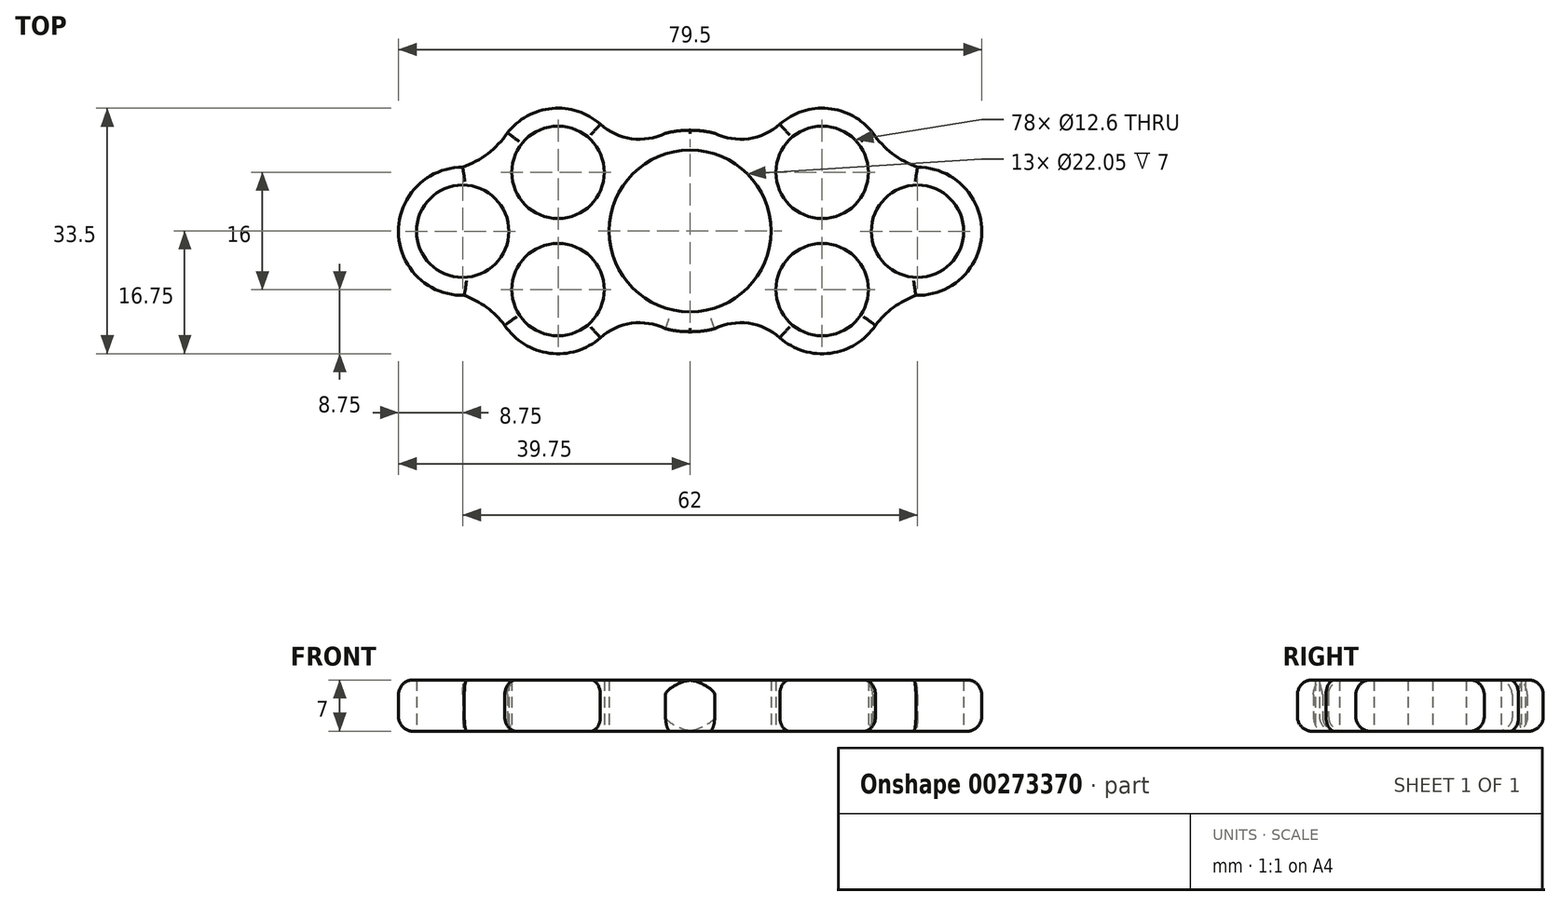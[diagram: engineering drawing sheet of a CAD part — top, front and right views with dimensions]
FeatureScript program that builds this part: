
annotation { "Feature Type Name" : "Feature", "Feature Type Description" : "" }
export const myFeature = defineFeature(function(context is Context, id is Id, definition is map)
    precondition{}
    {
        {
            var Q0;
            Q0=qCreatedBy(makeId("Top.planeOp"),FACE);
            var sketch = newSketch(context, id + "F0", { "sketchPlane" : qUnion([Q0])});
            skCircle(sketch, "E0", {"center": v(0, 0) * mm, "radius": 11.03 * mm});
            skCircle(sketch, "E1", {"center": v(18, 8) * mm, "radius": 6.3 * mm});
            skCircle(sketch, "E2.MirrorC", {"center": v(18, -8) * mm, "radius": 6.3 * mm});
            skLineSegment(sketch, "E3", {"start": v(18, -8) * mm, "end": v(18, 8) * mm, "construction": true});
            skCircle(sketch, "E4", {"center": v(31, -0.04) * mm, "radius": 6.3 * mm});
            skArc(sketch, "E5", {"start": v(3.35, 13.34) * mm, "mid": v(0, 13.75) * mm, "end": v(-3.35, 13.34) * mm});
            skArc(sketch, "E6", {"start": v(30.77, -8.79) * mm, "mid": v(39.75, -0.15) * mm, "end": v(31, 8.7) * mm});
            skArc(sketch, "E7", {"start": v(3.35, 13.34) * mm, "mid": v(7.98, 12.6) * mm, "end": v(12.23, 14.58) * mm});
            skArc(sketch, "E8", {"start": v(24.9, 13.38) * mm, "mid": v(27.58, 10.56) * mm, "end": v(31, 8.7) * mm});
            skArc(sketch, "E9.MirrorCS", {"start": v(3.35, -13.34) * mm, "mid": v(7.98, -12.6) * mm, "end": v(12.23, -14.58) * mm});
            skArc(sketch, "E10.MirrorCS", {"start": v(25.27, -12.86) * mm, "mid": v(27.74, -10.44) * mm, "end": v(30.77, -8.79) * mm});
            skArc(sketch, "E11.trimOffspring", {"start": v(24.9, 13.38) * mm, "mid": v(18.76, 16.72) * mm, "end": v(12.14, 14.5) * mm});
            skArc(sketch, "E12.trimOffspring", {"start": v(25.27, -12.86) * mm, "mid": v(19.08, -16.68) * mm, "end": v(12.14, -14.5) * mm});
            skPoint(sketch, "E13.orphan", {"position": v(31, -8.7) * mm});
            skPoint(sketch, "E14.orphan", {"position": v(24.9, -13.38) * mm});
            skPoint(sketch, "E15.MirrorP", {"position": v(-31, -8.7) * mm});
            skLineSegment(sketch, "E16.MirrorCS", {"start": v(-18, -8) * mm, "end": v(-18, 8) * mm, "construction": true});
            skCircle(sketch, "E17.MirrorC", {"center": v(-31, -0.04) * mm, "radius": 6.3 * mm});
            skPoint(sketch, "E18.MirrorP", {"position": v(-24.9, -13.38) * mm});
            skCircle(sketch, "E19.MirrorC", {"center": v(-18, -8) * mm, "radius": 6.3 * mm});
            skArc(sketch, "E20.MirrorCS", {"start": v(-24.9, 13.38) * mm, "mid": v(-27.58, 10.56) * mm, "end": v(-31, 8.7) * mm});
            skArc(sketch, "E21.MirrorCS", {"start": v(-3.35, -13.34) * mm, "mid": v(-7.98, -12.6) * mm, "end": v(-12.23, -14.58) * mm});
            skArc(sketch, "E22.MirrorCS", {"start": v(-24.9, 13.38) * mm, "mid": v(-18.76, 16.72) * mm, "end": v(-12.14, 14.5) * mm});
            skArc(sketch, "E23.MirrorCS", {"start": v(-25.27, -12.86) * mm, "mid": v(-19.08, -16.68) * mm, "end": v(-12.14, -14.5) * mm});
            skArc(sketch, "E24.MirrorCS", {"start": v(-3.35, 13.34) * mm, "mid": v(-7.98, 12.6) * mm, "end": v(-12.23, 14.58) * mm});
            skArc(sketch, "E25.MirrorCS", {"start": v(-25.27, -12.86) * mm, "mid": v(-27.74, -10.44) * mm, "end": v(-30.77, -8.79) * mm});
            skCircle(sketch, "E26.MirrorC", {"center": v(-18, 8) * mm, "radius": 6.3 * mm});
            skArc(sketch, "E27.MirrorCS", {"start": v(-30.77, -8.79) * mm, "mid": v(-39.75, -0.15) * mm, "end": v(-31, 8.7) * mm});
            skArc(sketch, "E28.trimOffspring", {"start": v(-3.35, -13.34) * mm, "mid": v(0, -13.75) * mm, "end": v(3.35, -13.34) * mm});
            skSolve(sketch);
        }
        {
            var Q0;
            Q0=makeQuery(id+"F0.imprint","IMPRINT",FACE,{"disambiguationData":[TD([[makeQuery(id+"F0.imprint","IMPRINT",EDGE,{"derivedFrom":sQuery(id+"F0.wireOp",EDGE,"E1")}),-1.0]])]});
            extrude(context, id + "F1", {"entities" : qUnion([Q0]), "depth" : 7 * mm});
        }
        {
            var Q0;
            Q0=makeQuery(id+"F1.opExtrude","CAP_EDGE",EDGE,{"disambiguationData":[OSD([sQuery(id+"F0.wireOp",EDGE,"E21.MirrorCS")])],"isStart":false});
            var Q1;
            Q1=makeQuery(id+"F1.opExtrude","CAP_EDGE",EDGE,{"disambiguationData":[OSD([sQuery(id+"F0.wireOp",EDGE,"E9.MirrorCS")])],"isStart":false});
            var Q2;
            Q2=makeQuery(id+"F1.opExtrude","CAP_EDGE",EDGE,{"disambiguationData":[OSD([sQuery(id+"F0.wireOp",EDGE,"E24.MirrorCS")])],"isStart":false});
            var Q3;
            Q3=makeQuery(id+"F1.opExtrude","CAP_EDGE",EDGE,{"disambiguationData":[OSD([sQuery(id+"F0.wireOp",EDGE,"E7")])],"isStart":false});
            var Q4;
            Q4=makeQuery(id+"F1.opExtrude","CAP_EDGE",EDGE,{"disambiguationData":[OSD([sQuery(id+"F0.wireOp",EDGE,"E21.MirrorCS")])],"isStart":true});
            var Q5;
            Q5=makeQuery(id+"F1.opExtrude","CAP_EDGE",EDGE,{"disambiguationData":[OSD([sQuery(id+"F0.wireOp",EDGE,"E9.MirrorCS")])],"isStart":true});
            var Q6;
            Q6=makeQuery(id+"F1.opExtrude","CAP_EDGE",EDGE,{"disambiguationData":[OSD([sQuery(id+"F0.wireOp",EDGE,"E24.MirrorCS")])],"isStart":true});
            var Q7;
            Q7=makeQuery(id+"F1.opExtrude","CAP_EDGE",EDGE,{"disambiguationData":[OSD([sQuery(id+"F0.wireOp",EDGE,"E7")])],"isStart":true});
            var Q8;
            Q8=makeQuery(id+"F1.opExtrude","CAP_EDGE",EDGE,{"disambiguationData":[OSD([sQuery(id+"F0.wireOp",EDGE,"E27.MirrorCS")])],"isStart":false});
            var Q9;
            Q9=makeQuery(id+"F1.opExtrude","CAP_EDGE",EDGE,{"disambiguationData":[OSD([sQuery(id+"F0.wireOp",EDGE,"E6")])],"isStart":false});
            var Q10;
            Q10=makeQuery(id+"F1.opExtrude","CAP_EDGE",EDGE,{"disambiguationData":[OSD([sQuery(id+"F0.wireOp",EDGE,"E27.MirrorCS")])],"isStart":true});
            var Q11;
            Q11=makeQuery(id+"F1.opExtrude","CAP_EDGE",EDGE,{"disambiguationData":[OSD([sQuery(id+"F0.wireOp",EDGE,"E6")])],"isStart":true});
            var Q12;
            Q12=makeQuery(id+"F1.opExtrude","CAP_EDGE",EDGE,{"disambiguationData":[OSD([sQuery(id+"F0.wireOp",EDGE,"E10.MirrorCS")])],"isStart":false});
            var Q13;
            Q13=makeQuery(id+"F1.opExtrude","CAP_EDGE",EDGE,{"disambiguationData":[OSD([sQuery(id+"F0.wireOp",EDGE,"E12.trimOffspring")])],"isStart":false});
            var Q14;
            Q14=makeQuery(id+"F1.opExtrude","CAP_EDGE",EDGE,{"disambiguationData":[OSD([sQuery(id+"F0.wireOp",EDGE,"E12.trimOffspring")])],"isStart":true});
            var Q15;
            Q15=makeQuery(id+"F1.opExtrude","CAP_EDGE",EDGE,{"disambiguationData":[OSD([sQuery(id+"F0.wireOp",EDGE,"E10.MirrorCS")])],"isStart":true});
            var Q16;
            Q16=makeQuery(id+"F1.opExtrude","CAP_EDGE",EDGE,{"disambiguationData":[OSD([sQuery(id+"F0.wireOp",EDGE,"E23.MirrorCS")])],"isStart":true});
            var Q17;
            Q17=makeQuery(id+"F1.opExtrude","CAP_EDGE",EDGE,{"disambiguationData":[OSD([sQuery(id+"F0.wireOp",EDGE,"E25.MirrorCS")])],"isStart":true});
            var Q18;
            Q18=makeQuery(id+"F1.opExtrude","CAP_EDGE",EDGE,{"disambiguationData":[OSD([sQuery(id+"F0.wireOp",EDGE,"E23.MirrorCS")])],"isStart":false});
            var Q19;
            Q19=makeQuery(id+"F1.opExtrude","CAP_EDGE",EDGE,{"disambiguationData":[OSD([sQuery(id+"F0.wireOp",EDGE,"E25.MirrorCS")])],"isStart":false});
            var Q20;
            Q20=makeQuery(id+"F1.opExtrude","CAP_EDGE",EDGE,{"disambiguationData":[OSD([sQuery(id+"F0.wireOp",EDGE,"E20.MirrorCS")])],"isStart":false});
            var Q21;
            Q21=makeQuery(id+"F1.opExtrude","CAP_EDGE",EDGE,{"disambiguationData":[OSD([sQuery(id+"F0.wireOp",EDGE,"E22.MirrorCS")])],"isStart":false});
            var Q22;
            Q22=makeQuery(id+"F1.opExtrude","CAP_EDGE",EDGE,{"disambiguationData":[OSD([sQuery(id+"F0.wireOp",EDGE,"E11.trimOffspring")])],"isStart":false});
            var Q23;
            Q23=makeQuery(id+"F1.opExtrude","CAP_EDGE",EDGE,{"disambiguationData":[OSD([sQuery(id+"F0.wireOp",EDGE,"E8")])],"isStart":false});
            var Q24;
            Q24=makeQuery(id+"F1.opExtrude","CAP_EDGE",EDGE,{"disambiguationData":[OSD([sQuery(id+"F0.wireOp",EDGE,"E8")])],"isStart":true});
            var Q25;
            Q25=makeQuery(id+"F1.opExtrude","CAP_EDGE",EDGE,{"disambiguationData":[OSD([sQuery(id+"F0.wireOp",EDGE,"E11.trimOffspring")])],"isStart":true});
            var Q26;
            Q26=makeQuery(id+"F1.opExtrude","CAP_EDGE",EDGE,{"disambiguationData":[OSD([sQuery(id+"F0.wireOp",EDGE,"E22.MirrorCS")])],"isStart":true});
            var Q27;
            Q27=makeQuery(id+"F1.opExtrude","CAP_EDGE",EDGE,{"disambiguationData":[OSD([sQuery(id+"F0.wireOp",EDGE,"E28.trimOffspring")])],"isStart":true});
            var Q28;
            Q28=makeQuery(id+"F1.opExtrude","CAP_EDGE",EDGE,{"disambiguationData":[OSD([sQuery(id+"F0.wireOp",EDGE,"E20.MirrorCS")])],"isStart":true});
            fillet(context, id + "F2", {"entities" : qUnion([Q0, Q1, Q2, Q3, Q4, Q5, Q6, Q7, Q8, Q9, Q10, Q11, Q12, Q13, Q14, Q15, Q16, Q17, Q18, Q19, Q20, Q21, Q22, Q23, Q24, Q25, Q26, Q27, Q28]), "radius" : 2 * mm, "tangentPropagation" : true, "allowEdgeOverflow" : false});
        }
    });
